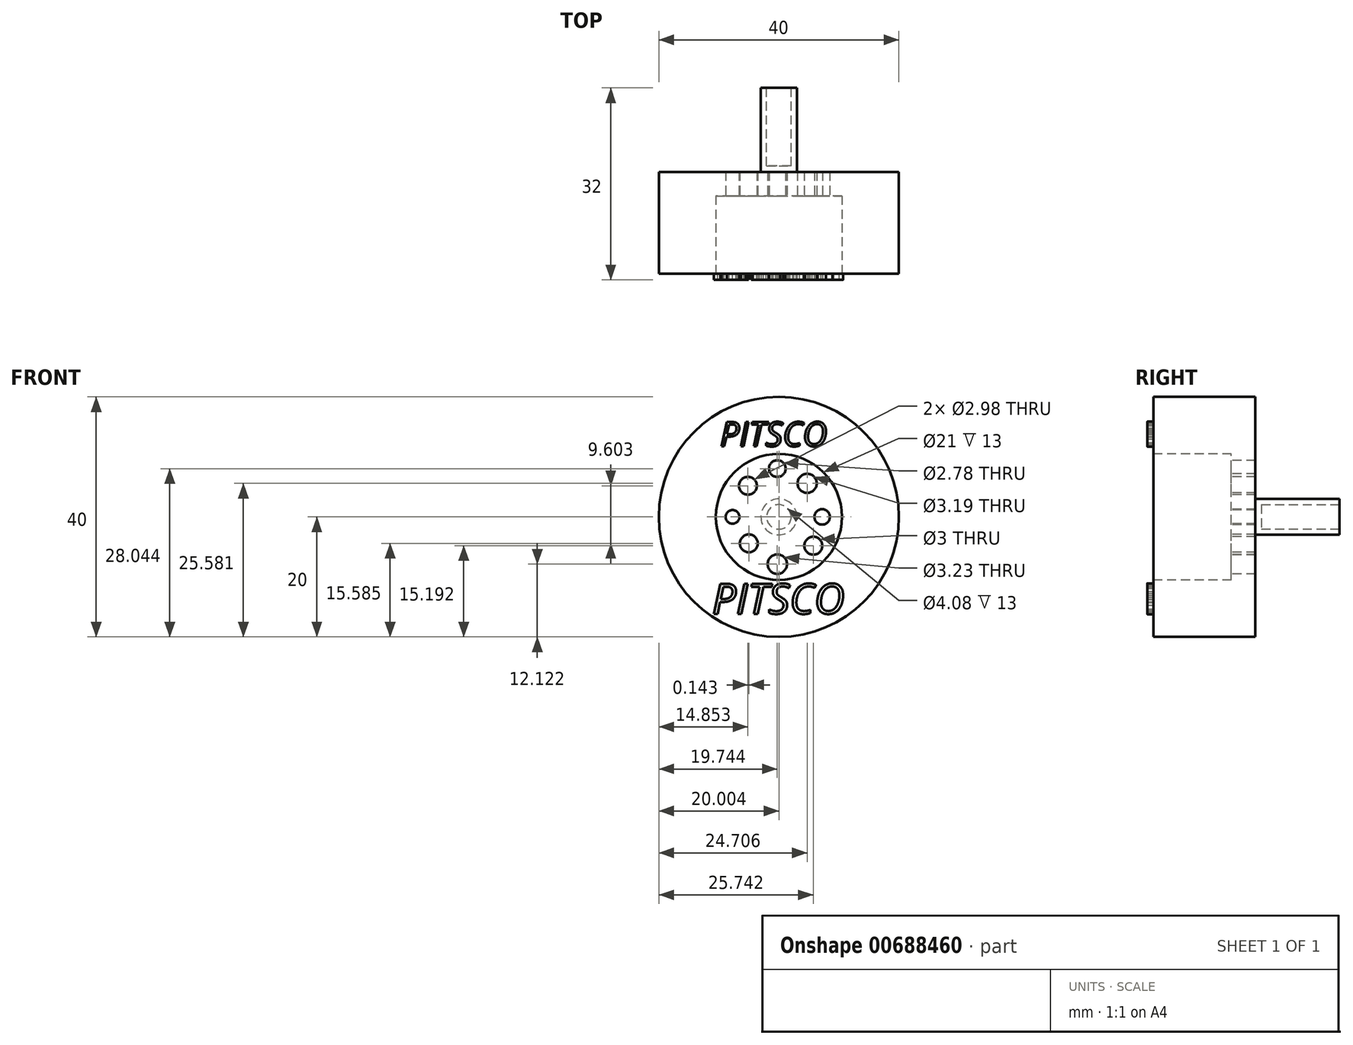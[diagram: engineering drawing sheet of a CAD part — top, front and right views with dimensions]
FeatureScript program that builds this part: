
annotation { "Feature Type Name" : "Feature", "Feature Type Description" : "" }
export const myFeature = defineFeature(function(context is Context, id is Id, definition is map)
    precondition{}
    {
        {
            var Q0;
            Q0=qCreatedBy(makeId("Front.planeOp"),FACE);
            var sketch = newSketch(context, id + "F0", { "sketchPlane" : qUnion([Q0])});
            skCircle(sketch, "E0", {"center": v(26.8, 0) * mm, "radius": 20 * mm});
            skLineSegment(sketch, "E1", {"start": v(6.8, 0) * mm, "end": v(46.8, 0) * mm});
            skSolve(sketch);
        }
        {
            var Q0;
            {var subQ0=sQuery(id+"F0.wireOp",EDGE,"E1");Q0=makeQuery(id+"F0.imprint","IMPRINT",FACE,{"disambiguationData":[TD([[makeQuery(id+"F0.imprint","IMPRINT",EDGE,{"derivedFrom":subQ0}),-1.0]])]});}
            var Q1;
            {var subQ0=sQuery(id+"F0.wireOp",EDGE,"E1");Q1=makeQuery(id+"F0.imprint","IMPRINT",FACE,{"disambiguationData":[TD([[makeQuery(id+"F0.imprint","IMPRINT",EDGE,{"derivedFrom":subQ0}),1.0]])]});}
            extrude(context, id + "F1", {"entities" : qUnion([Q0, Q1]), "depth" : 17 * mm, "offsetDistance" : 25 * mm});
        }
        {
            var Q0;
            Q0=makeQuery(id+"F1.opExtrude","CAP_FACE",FACE,{"disambiguationData":[OSD([sQuery(id+"F0.wireOp",EDGE,"E0")])],"isStart":false});
            var sketch = newSketch(context, id + "F2", { "sketchPlane" : qUnion([Q0])});
            skCircle(sketch, "E2", {"center": v(26.8, 0) * mm, "radius": 10.5 * mm});
            skLineSegment(sketch, "E3", {"start": v(16.3, 0) * mm, "end": v(37.3, 0) * mm});
            skSolve(sketch);
        }
        {
            var Q0;
            {var subQ0=sQuery(id+"F2.wireOp",EDGE,"E3");Q0=makeQuery(id+"F2.imprint","IMPRINT",FACE,{"disambiguationData":[TD([[makeQuery(id+"F2.imprint","IMPRINT",EDGE,{"derivedFrom":subQ0}),1.0]])]});}
            var Q1;
            {var subQ0=sQuery(id+"F2.wireOp",EDGE,"E3");Q1=makeQuery(id+"F2.imprint","IMPRINT",FACE,{"disambiguationData":[TD([[makeQuery(id+"F2.imprint","IMPRINT",EDGE,{"derivedFrom":subQ0}),-1.0]])]});}
            extrude(context, id + "F3", {"entities" : qUnion([Q0, Q1]), "operationType" : NewBodyOperationType.REMOVE, "oppositeDirection" : true, "depth" : 13 * mm, "offsetDistance" : 25 * mm});
        }
        {
            var Q0;
            Q0=makeQuery(id+"F1.opExtrude","CAP_FACE",FACE,{"disambiguationData":[OSD([sQuery(id+"F0.wireOp",EDGE,"E0")])],"isStart":true});
            var sketch = newSketch(context, id + "F4", { "sketchPlane" : qUnion([Q0])});
            skCircle(sketch, "E4", {"center": v(-26.8, 0) * mm, "radius": 3 * mm});
            skLineSegment(sketch, "E5", {"start": v(-29.8, 0) * mm, "end": v(-23.8, 0) * mm});
            skSolve(sketch);
        }
        {
            var Q0;
            {var subQ0=sQuery(id+"F4.wireOp",EDGE,"E5");Q0=makeQuery(id+"F4.imprint","IMPRINT",FACE,{"disambiguationData":[TD([[makeQuery(id+"F4.imprint","IMPRINT",EDGE,{"derivedFrom":subQ0}),1.0]])]});}
            var Q1;
            {var subQ0=sQuery(id+"F4.wireOp",EDGE,"E5");Q1=makeQuery(id+"F4.imprint","IMPRINT",FACE,{"disambiguationData":[TD([[makeQuery(id+"F4.imprint","IMPRINT",EDGE,{"derivedFrom":subQ0}),-1.0]])]});}
            extrude(context, id + "F5", {"entities" : qUnion([Q0, Q1]), "operationType" : NewBodyOperationType.ADD, "depth" : 14 * mm, "offsetDistance" : 25 * mm});
        }
        {
            var Q0;
            Q0=makeQuery(id+"F3.boolean.opBoolean","COPY",FACE,{"derivedFrom":makeQuery(id+"F3.opExtrude","CAP_FACE",FACE,{"disambiguationData":[OSD([sQuery(id+"F2.wireOp",EDGE,"E2")])],"isStart":false})});
            var sketch = newSketch(context, id + "F6", { "sketchPlane" : qUnion([Q0])});
            skCircle(sketch, "E6", {"center": v(26.53, 8.04) * mm, "radius": 1.4 * mm});
            skCircle(sketch, "E7", {"center": v(34, 0) * mm, "radius": 1.29 * mm});
            skCircle(sketch, "E8", {"center": v(26.53, -7.88) * mm, "radius": 1.61 * mm});
            skCircle(sketch, "E9", {"center": v(19.07, 0) * mm, "radius": 1.14 * mm});
            skCircle(sketch, "E10", {"center": v(21.79, -4.42) * mm, "radius": 1.5 * mm});
            skCircle(sketch, "E11", {"center": v(32.53, -4.8) * mm, "radius": 1.5 * mm});
            skCircle(sketch, "E12", {"center": v(31.5, 5.58) * mm, "radius": 1.6 * mm});
            skCircle(sketch, "E13", {"center": v(21.64, 5.19) * mm, "radius": 1.49 * mm});
            skSolve(sketch);
        }
        {
            var Q0;
            Q0 = qSketchRegion(id + "F6", true);
            extrude(context, id + "F7", {"entities" : qUnion([Q0]), "operationType" : NewBodyOperationType.REMOVE, "oppositeDirection" : true, "depth" : 25 * mm, "offsetDistance" : 25 * mm});
        }
        {
            var Q0;
            Q0=makeQuery(id+"F1.opExtrude","CAP_FACE",FACE,{"disambiguationData":[OSD([sQuery(id+"F0.wireOp",EDGE,"E0")])],"isStart":false});
            var sketch = newSketch(context, id + "F8", { "sketchPlane" : qUnion([Q0])});
            skText(sketch, "E14", { "text": "PITSCO", "fontName": "OpenSans-Italic.ttf"});
            const initialGuessF8  = {"E14": [0.017, 0.01177, 1, 0, 0.00408]};
            skSetInitialGuess(sketch, initialGuessF8);
            skSolve(sketch);
        }
        {
            var Q0;
            Q0=makeQuery(id+"F8.imprint","IMPRINT",FACE,{"disambiguationData":[TD([[makeQuery(id+"F8.imprint","IMPRINT",EDGE,{"derivedFrom":sQuery(id+"F8.wireOp",EDGE,"E14.sketch_text.stroke-0")}),1.0]])]});
            var sketch = newSketch(context, id + "F9", { "sketchPlane" : qUnion([Q0])});
            skText(sketch, "E15", { "text": "PITSCO", "fontName": "OpenSans-Italic.ttf"});
            const initialGuessF9  = {"E15": [0.0157, -0.01615, 1, 0, 0.00504]};
            skSetInitialGuess(sketch, initialGuessF9);
            skSolve(sketch);
        }
        {
            var Q0;
            Q0 = qSketchRegion(id + "F9", true);
            var Q1;
            Q1 = qSketchRegion(id + "F8", true);
            extrude(context, id + "F10", {"entities" : qUnion([Q0, Q1]), "operationType" : NewBodyOperationType.ADD, "depth" : 1 * mm, "offsetDistance" : 25 * mm});
        }
        {
            var Q0;
            Q0=makeQuery(id+"F5.opExtrude","CAP_FACE",FACE,{"disambiguationData":[OSD([sQuery(id+"F4.wireOp",EDGE,"E4")])],"isStart":false});
            var sketch = newSketch(context, id + "F11", { "sketchPlane" : qUnion([Q0])});
            skCircle(sketch, "E16", {"center": v(-26.8, 0) * mm, "radius": 2.1 * mm});
            skSolve(sketch);
        }
        {
            var Q0;
            Q0=makeQuery(id+"F11.imprint","IMPRINT",FACE,{"disambiguationData":[TD([[makeQuery(id+"F11.imprint","IMPRINT",EDGE,{"derivedFrom":sQuery(id+"F11.wireOp",EDGE,"E16")}),1.0]])]});
            extrude(context, id + "F12", {"entities" : qUnion([Q0]), "operationType" : NewBodyOperationType.REMOVE, "depth" : 13 * mm, "offsetDistance" : 25 * mm});
        }
        {
            var Q0;
            Q0=makeQuery(id+"F5.opExtrude","CAP_FACE",FACE,{"disambiguationData":[OSD([sQuery(id+"F4.wireOp",EDGE,"E4")])],"isStart":false});
            var sketch = newSketch(context, id + "F13", { "sketchPlane" : qUnion([Q0])});
            skCircle(sketch, "E17", {"center": v(-26.8, 0) * mm, "radius": 2.04 * mm});
            skSolve(sketch);
        }
        {
            var Q0;
            Q0 = qSketchRegion(id + "F13", true);
            extrude(context, id + "F14", {"entities" : qUnion([Q0]), "operationType" : NewBodyOperationType.REMOVE, "oppositeDirection" : true, "depth" : 13 * mm, "offsetDistance" : 25 * mm});
        }
    });
